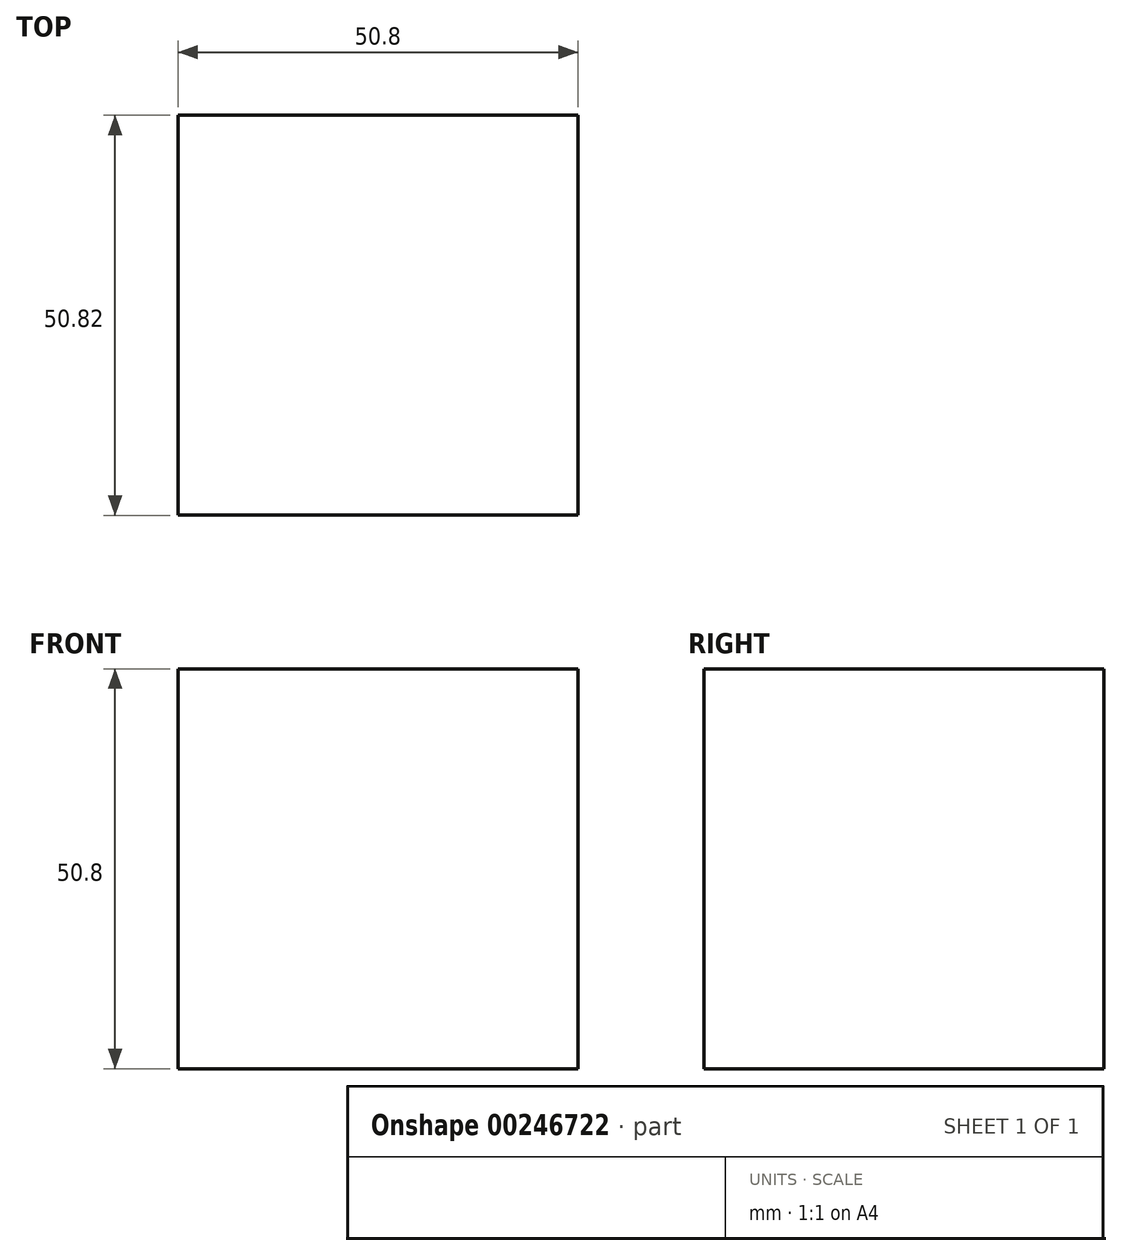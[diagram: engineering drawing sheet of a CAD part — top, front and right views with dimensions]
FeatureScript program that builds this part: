
annotation { "Feature Type Name" : "Feature", "Feature Type Description" : "" }
export const myFeature = defineFeature(function(context is Context, id is Id, definition is map)
    precondition{}
    {
        {
            var Q0;
            Q0=qCreatedBy(makeId("Top.planeOp"),FACE);
            var sketch = newSketch(context, id + "F0", { "sketchPlane" : qUnion([Q0])});
            skLineSegment(sketch, "E0.bottom", {"start": v(-25.4, 25.4) * mm, "end": v(25.4, 25.4) * mm});
            skLineSegment(sketch, "E0.top", {"start": v(-25.4, -25.4) * mm, "end": v(25.4, -25.4) * mm});
            skLineSegment(sketch, "E0.left", {"start": v(-25.4, 25.4) * mm, "end": v(-25.4, -25.4) * mm});
            skLineSegment(sketch, "E0.right", {"start": v(25.4, 25.4) * mm, "end": v(25.4, -25.4) * mm});
            skPoint(sketch, "E0.middle", {"position": v(0, 0) * mm});
            skSolve(sketch);
        }
        {
            var Q0;
            Q0 = qSketchRegion(id + "F0", true);
            extrude(context, id + "F1", {"entities" : qUnion([Q0]), "depth" : 50.8 * mm});
        }
    });
